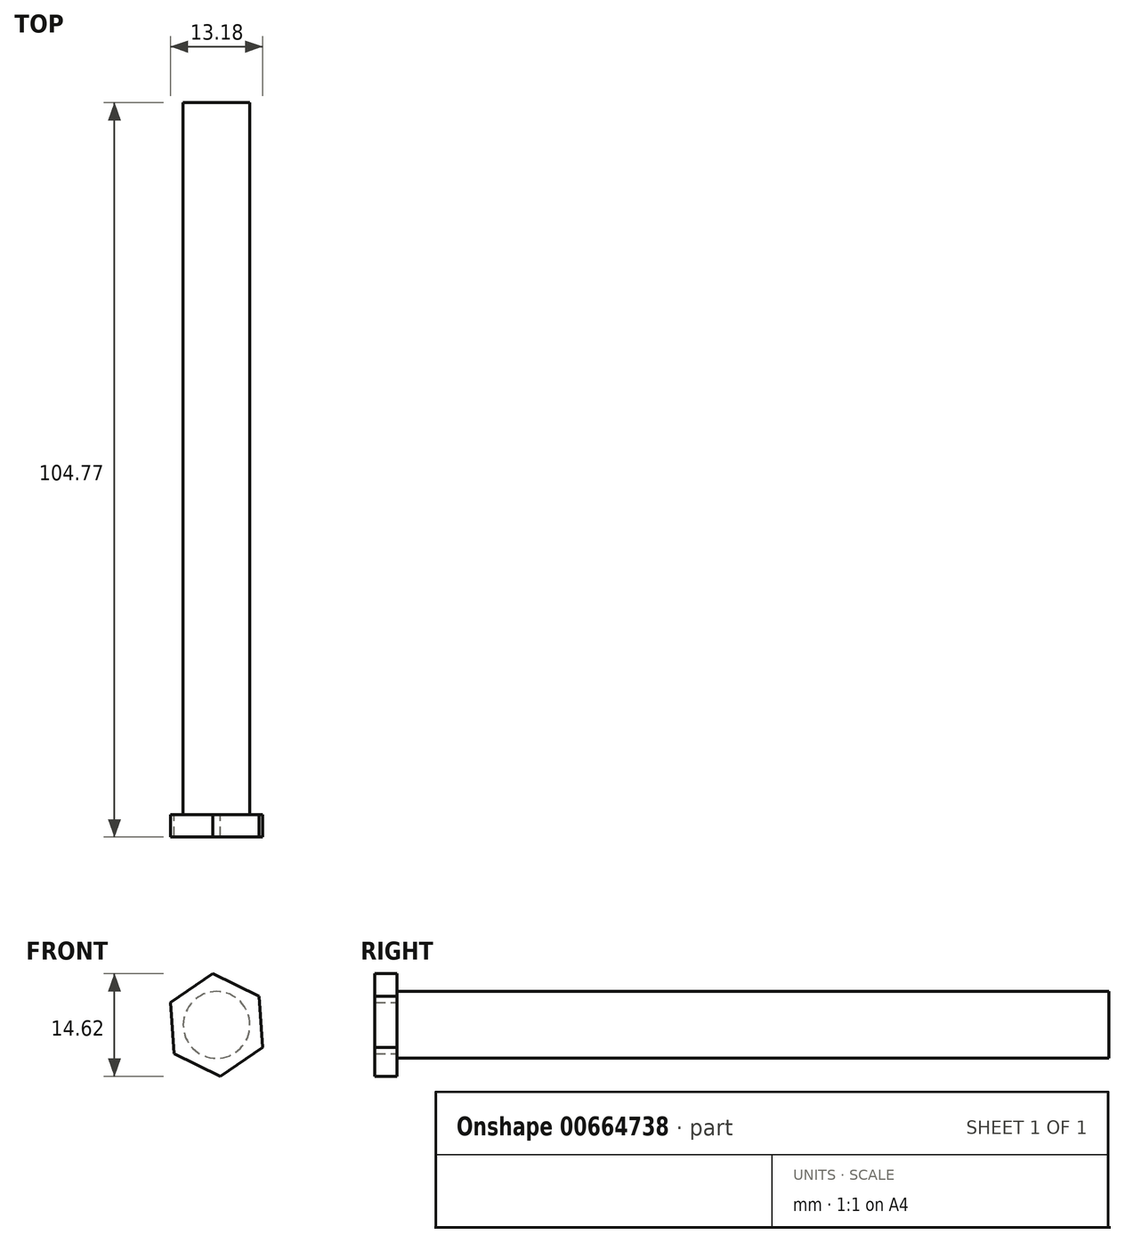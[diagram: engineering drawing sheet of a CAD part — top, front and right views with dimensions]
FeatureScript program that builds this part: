
annotation { "Feature Type Name" : "Feature", "Feature Type Description" : "" }
export const myFeature = defineFeature(function(context is Context, id is Id, definition is map)
    precondition{}
    {
        {
            var Q0;
            Q0=qCreatedBy(makeId("Front.planeOp"),FACE);
            var sketch = newSketch(context, id + "F0", { "sketchPlane" : qUnion([Q0])});
            skCircle(sketch, "E0", {"center": v(0, 0) * mm, "radius": 4.76 * mm});
            skSolve(sketch);
        }
        {
            var Q0;
            Q0 = qSketchRegion(id + "F0", true);
            extrude(context, id + "F1", {"entities" : qUnion([Q0]), "depth" : 101.6 * mm, "offsetDistance" : 25.4 * mm});
        }
        {
            var Q0;
            Q0=makeQuery(id+"F1.opExtrude","CAP_FACE",FACE,{"disambiguationData":[OSD([sQuery(id+"F0.wireOp",EDGE,"E0")])],"isStart":false});
            var sketch = newSketch(context, id + "F2", { "sketchPlane" : qUnion([Q0])});
            skCircle(sketch, "E1.cCircle", {"center": v(0, 0) * mm, "radius": 7.33 * mm, "construction": true});
            skLineSegment(sketch, "E1.0", {"start": v(6.6, -3.21) * mm, "end": v(0.51, -7.31) * mm});
            skLineSegment(sketch, "E1.1", {"start": v(0.51, -7.31) * mm, "end": v(-6.08, -4.1) * mm});
            skLineSegment(sketch, "E1.2", {"start": v(-6.08, -4.1) * mm, "end": v(-6.6, 3.21) * mm});
            skLineSegment(sketch, "E1.3", {"start": v(-6.6, 3.21) * mm, "end": v(-0.51, 7.31) * mm});
            skLineSegment(sketch, "E1.4", {"start": v(-0.51, 7.31) * mm, "end": v(6.08, 4.1) * mm});
            skLineSegment(sketch, "E1.5", {"start": v(6.08, 4.1) * mm, "end": v(6.6, -3.21) * mm});
            skSolve(sketch);
        }
        {
            var Q0;
            Q0 = qSketchRegion(id + "F2", true);
            extrude(context, id + "F3", {"entities" : qUnion([Q0]), "operationType" : NewBodyOperationType.ADD, "depth" : 3.17 * mm, "offsetDistance" : 25.4 * mm});
        }
    });
